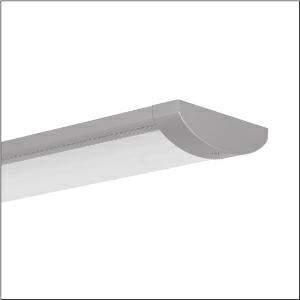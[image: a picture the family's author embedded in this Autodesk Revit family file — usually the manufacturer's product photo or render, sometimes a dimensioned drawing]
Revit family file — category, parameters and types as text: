
# Revit family: tv_20_5xa86174n0x
name_source: partatom
category: Lighting Fixtures
units: mm (PartAtom-declared; Revit-internal decimal feet)

## family parameters
Cut with Voids When Loaded = No
Host = Face
Light Source = No
Part Type = Normal
Room Calculation Point = No
Round Connector Dimension = Use Diameter
Shared = No

## types (1)
- TV 20 (1 x LED 4000K / CRI = 80 (unbekannt), 5120 lm, 4000K)
    Apparent Load = 50 VA
    CIE Flux Codes = 48 78 95 99 100
    Color Rendering = 80
    Color Temperature = 4000K
    Default Elevation = 1800 mm
    Description = TV 20, vandal-proof luminaire, primary light control with specular reflector, of aluminium, matt, primary optical cover: enclosure, of PC, frosted, light emission: direct distribution, primary light characteristic: symmetric, installation type: surface-mounted, LED, rated luminous flux: 5.120lm, luminous efficacy: 102lm/W, light colour: 840, colour temperature: 4000K, control gear: ECG, mains connection: 230V, AC, 50Hz, rated input power: 50W, luminaire housing, of aluminium, coated, Siteco® metallic grey (DB 702S), with wall and ceiling fixing element, length: 1.561mm, width: 260mm, height: 70mm, protection rating (complete): IP65, insulation class (complete): insulation class I (protective earthing), certification: CE, protection symbol: F, impact resistance: 2x IK10, standard: EN 60598, packaging unit: 1 piece
    Height = 70 mm
    Lamp = 1 x LED 4000K / CRI >= 80 (unbekannt)
    Lamp Light Flux = 5120 lm
    Lamp count = 1
    Length = 1561 mm
    Luminous efficacy = 102 lm/W
    Manufacturer = Siteco
    ModVariant = No
    Model = 5XA86174N0X
    Mounting Place = Ceiling
    Mounting Type = Surface mounted
    Number of Poles = 1
    OnlyDefault = Yes
    Power Factor = 1
    Product Name = TV 20
    Product group = vandal-proof luminaire
    ProductGroupID = 307
    Protection Class = Protection class I
    Protection Degree = IP 65
    RLX_Detail_Level = 1
    RLX_Emergency_Light_Flux = 0 lm
    RLX_Emergency_Type = 0
    RLX_Emergency_Type_DB = No
    RlxData = <blob elided: 25237 chars, md5=47b9456b>
    Socket = socket
    Standby Power = 0 W
    System Light Flux = 5120 lm
    System Power = 50 W
    Type Comments = Product without accessories
    Type Image = l_1004809.jpg
    URL = http://relux.com
    VarID = ---
    Voltage = 0 V
    Weight = 0.00 kg
    Width = 260 mm

## geometry (parser evidence)
native form markers: Blend x4, Sweep x10
no freeform markers — native parametric forms only
